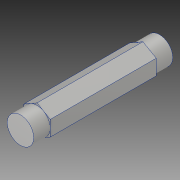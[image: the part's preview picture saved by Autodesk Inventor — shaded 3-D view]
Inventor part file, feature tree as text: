
AUTODESK INVENTOR PART (.ipt)
format: ipt  version: 2019 (Build 230136000, 136)  size: 120,320 bytes
history: native  units: in
note: dims shown in document units (in); Inventor stores cm internally (conversion verified against a paired STEP export)
features: extrude x2, sketch x2, mirror x1, projected_geometry x1
ambient origin geometry x8: Origin, YZ Plane, XZ Plane, XY Plane, X Axis, Y Axis, Z Axis, Center Point
bodies: Solid1 (feature_tree)
feature tree (6):
  extrude  "Extrusion1"  TaperAngle=0.0deg  [1 undecoded]
  extrude  "Extrusion2"  [1 undecoded]
  mirror  "Mirror1"
  sketch  "Sketch1"  dims[d2=0.0in d4=0.0in]
  sketch  "Sketch2"
  projected_geometry  "Projected Loop1"
note: 2 required parameter values undecoded (feature->parameter linkage not recoverable at this tier; creation-order binding heuristic only, values carry confidence <= 0.55)
